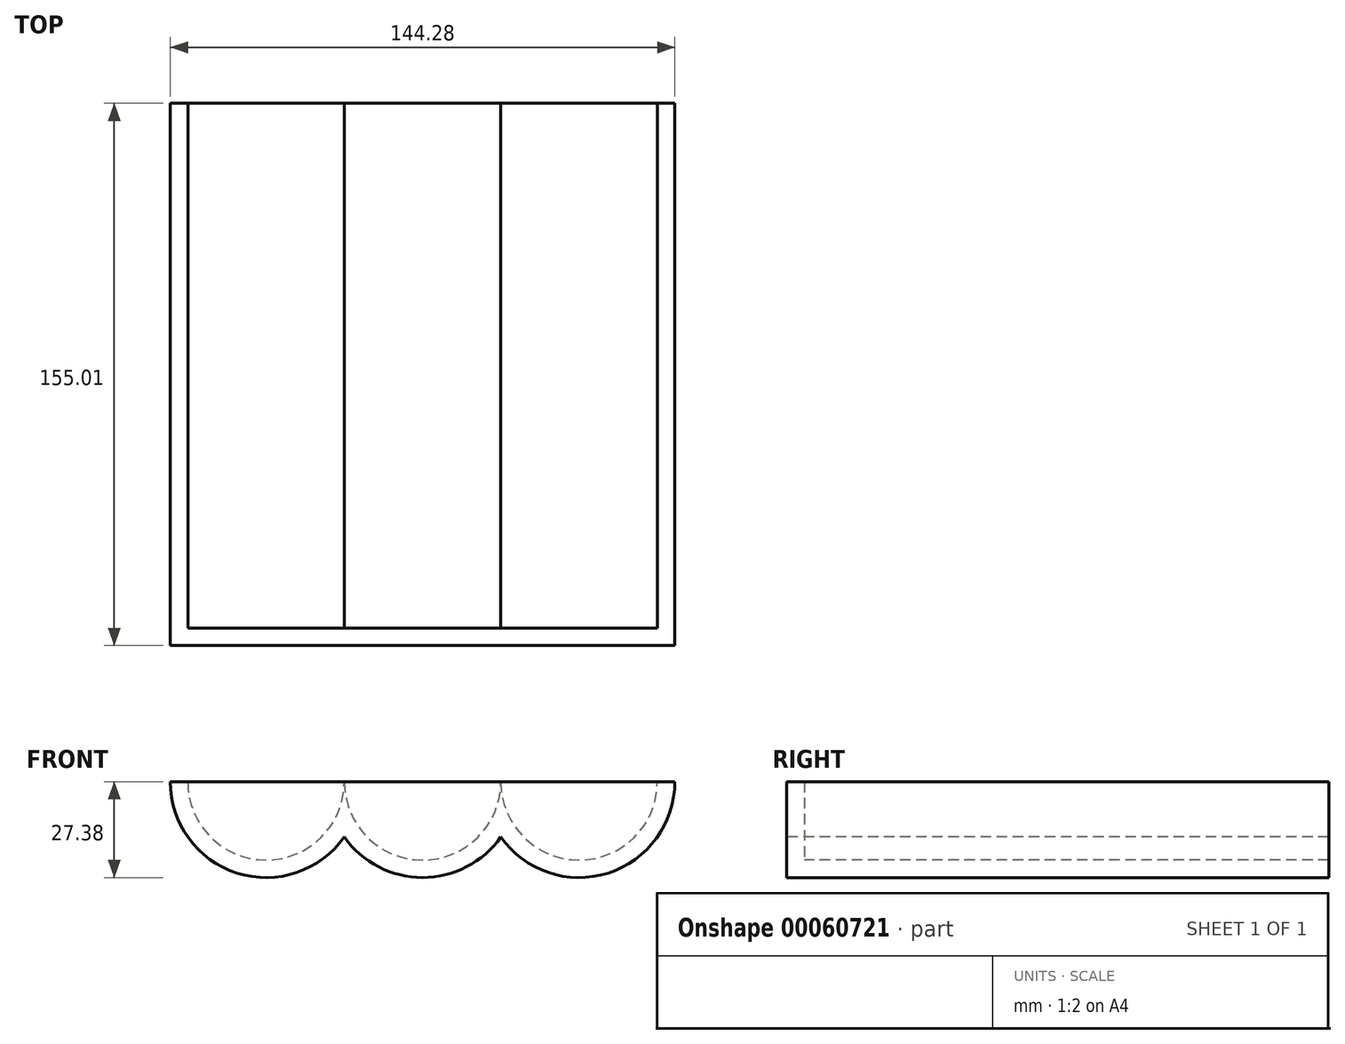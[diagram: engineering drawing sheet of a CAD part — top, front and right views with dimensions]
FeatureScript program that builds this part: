
annotation { "Feature Type Name" : "Feature", "Feature Type Description" : "" }
export const myFeature = defineFeature(function(context is Context, id is Id, definition is map)
    precondition{}
    {
        {
            var Q0;
            Q0=qCreatedBy(makeId("Front.planeOp"),FACE);
            var sketch = newSketch(context, id + "F0", { "sketchPlane" : qUnion([Q0])});
            skArc(sketch, "E0", {"start": v(-111.9, 0) * mm, "mid": v(-89.52, -22.38) * mm, "end": v(-67.14, 0) * mm});
            skArc(sketch, "E1", {"start": v(-67.14, 0) * mm, "mid": v(-44.76, -22.38) * mm, "end": v(-22.38, 0) * mm});
            skArc(sketch, "E2", {"start": v(-22.38, 0) * mm, "mid": v(0, -22.38) * mm, "end": v(22.38, 0) * mm});
            skArc(sketch, "E3.0", {"start": v(-22.38, -15.77) * mm, "mid": v(8.27, -26.1) * mm, "end": v(27.38, 0) * mm});
            skArc(sketch, "E3.1", {"start": v(-67.14, -15.77) * mm, "mid": v(-44.76, -27.38) * mm, "end": v(-22.38, -15.77) * mm});
            skArc(sketch, "E3.2", {"start": v(-116.9, 0) * mm, "mid": v(-97.8, -26.1) * mm, "end": v(-67.14, -15.77) * mm});
            skLineSegment(sketch, "E4", {"start": v(-116.9, 0) * mm, "end": v(-111.9, 0) * mm});
            skLineSegment(sketch, "E5", {"start": v(22.38, 0) * mm, "end": v(27.38, 0) * mm});
            skSolve(sketch);
        }
        {
            var Q0;
            Q0=makeQuery(id+"F0.imprint","IMPRINT",FACE,{"disambiguationData":[TD([[makeQuery(id+"F0.imprint","IMPRINT",EDGE,{"derivedFrom":sQuery(id+"F0.wireOp",EDGE,"E0")}),-1.0]])]});
            extrude(context, id + "F1", {"entities" : qUnion([Q0]), "oppositeDirection" : true, "depth" : 150 * mm});
        }
        {
            var Q0;
            Q0=makeQuery(id+"F1.opExtrude","CAP_FACE",FACE,{"disambiguationData":[OSD([sQuery(id+"F0.wireOp",EDGE,"E0"),sQuery(id+"F0.wireOp",EDGE,"E1"),sQuery(id+"F0.wireOp",EDGE,"E2"),sQuery(id+"F0.wireOp",EDGE,"E3.0"),sQuery(id+"F0.wireOp",EDGE,"E3.1"),sQuery(id+"F0.wireOp",EDGE,"E3.2"),sQuery(id+"F0.wireOp",EDGE,"E4"),sQuery(id+"F0.wireOp",EDGE,"E5")])],"isStart":true});
            var sketch = newSketch(context, id + "F2", { "sketchPlane" : qUnion([Q0])});
            skLineSegment(sketch, "E6.right", {"start": v(27.38, 0) * mm, "end": v(27.38, 0) * mm});
            skPoint(sketch, "E7.endSnap0", {"position": v(8.27, -26.1) * mm});
            skPoint(sketch, "E8", {"position": v(-114.4, 0) * mm});
            skLineSegment(sketch, "E9", {"start": v(-116.9, 0) * mm, "end": v(27.38, 0) * mm});
            skArc(sketch, "E10", {"start": v(-116.9, 0) * mm, "mid": v(-97.8, -26.1) * mm, "end": v(-67.14, -15.77) * mm});
            skArc(sketch, "E11", {"start": v(-67.14, -15.77) * mm, "mid": v(-44.76, -27.38) * mm, "end": v(-22.38, -15.77) * mm});
            skArc(sketch, "E12", {"start": v(-22.38, -15.77) * mm, "mid": v(8.27, -26.1) * mm, "end": v(27.38, 0) * mm});
            skSolve(sketch);
        }
        {
            var Q0;
            Q0 = qSketchRegion(id + "F2", true);
            extrude(context, id + "F3", {"entities" : qUnion([Q0]), "operationType" : NewBodyOperationType.ADD, "depth" : 5 * mm});
        }
        {
            var Q0;
            Q0=makeQuery(id+"F3.opExtrude","CAP_FACE",FACE,{"disambiguationData":[OSD([sQuery(id+"F2.wireOp",EDGE,"E9"),sQuery(id+"F2.wireOp",EDGE,"E10"),sQuery(id+"F2.wireOp",EDGE,"E11"),sQuery(id+"F2.wireOp",EDGE,"E12")])],"isStart":false});
            var sketch = newSketch(context, id + "F4", { "sketchPlane" : qUnion([Q0])});
            skLineSegment(sketch, "E13.bottom", {"start": v(-127.6, 19.48) * mm, "end": v(32.2, 19.48) * mm});
            skLineSegment(sketch, "E13.top", {"start": v(-127.6, -7.19) * mm, "end": v(32.2, -7.19) * mm});
            skLineSegment(sketch, "E13.left", {"start": v(-127.6, 19.48) * mm, "end": v(-127.6, -7.19) * mm});
            skLineSegment(sketch, "E13.right", {"start": v(32.2, 19.48) * mm, "end": v(32.2, -7.19) * mm});
            skSolve(sketch);
        }
        {
            var Q0;
            Q0=makeQuery(id+"F4.imprint","IMPRINT",FACE,{"disambiguationData":[TD([[makeQuery(id+"F4.imprint","IMPRINT",EDGE,{"derivedFrom":sQuery(id+"F4.wireOp",EDGE,"E13.bottom")}),-1.0]])]});
            var Q1;
            Q1=makeQuery(id+"F1.opExtrude","SWEPT_FACE",FACE,{"disambiguationData":[OSD([sQuery(id+"F0.wireOp",EDGE,"E2")])]});
            extrude(context, id + "F5", {"entities" : qUnion([Q0]), "operationType" : NewBodyOperationType.REMOVE, "oppositeDirection" : true, "endBoundEntityFace" : qUnion([Q1]), "depth" : 165.36 * mm});
        }
    });
